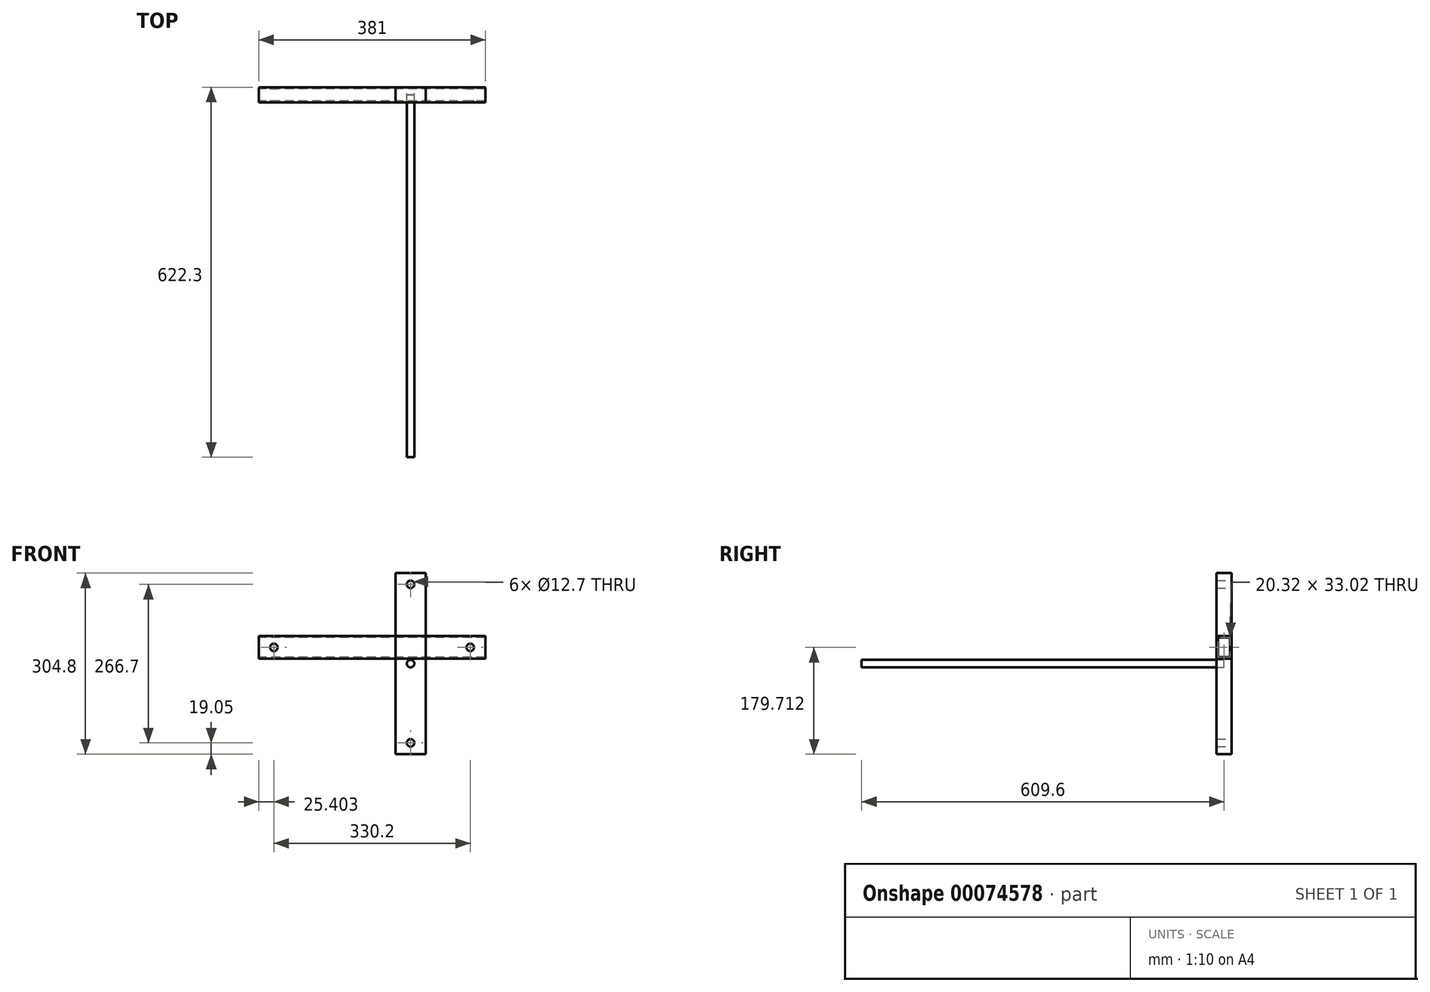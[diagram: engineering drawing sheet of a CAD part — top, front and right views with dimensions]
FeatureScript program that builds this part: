
annotation { "Feature Type Name" : "Feature", "Feature Type Description" : "" }
export const myFeature = defineFeature(function(context is Context, id is Id, definition is map)
    precondition{}
    {
        {
            var Q0;
            Q0=qCreatedBy(makeId("Front.planeOp"),FACE);
            var sketch = newSketch(context, id + "F0", { "sketchPlane" : qUnion([Q0])});
            skLineSegment(sketch, "E0.rect.bottom", {"start": v(25.4, 152.4) * mm, "end": v(-25.4, 152.4) * mm});
            skLineSegment(sketch, "E0.rect.top", {"start": v(25.4, -152.4) * mm, "end": v(-25.4, -152.4) * mm});
            skLineSegment(sketch, "E0.rect.left", {"start": v(25.4, 152.4) * mm, "end": v(25.4, -152.4) * mm});
            skLineSegment(sketch, "E0.rect.right", {"start": v(-25.4, 152.4) * mm, "end": v(-25.4, -152.4) * mm});
            skPoint(sketch, "E0.rect.middle", {"position": v(0, 0) * mm});
            skCircle(sketch, "E1", {"center": v(0, -133.35) * mm, "radius": 6.35 * mm});
            skCircle(sketch, "E2", {"center": v(0, 133.35) * mm, "radius": 6.35 * mm});
            skSolve(sketch);
        }
        {
            var Q0;
            Q0=makeQuery(id+"F0.imprint","IMPRINT",FACE,{"disambiguationData":[TD([[makeQuery(id+"F0.imprint","IMPRINT",EDGE,{"derivedFrom":sQuery(id+"F0.wireOp",EDGE,"E0.rect.bottom")}),1.0]])]});
            extrude(context, id + "F1", {"entities" : qUnion([Q0]), "endBound" : BoundingType.SYMMETRIC, "depth" : 25.4 * mm});
        }
        {
            var Q0;
            Q0=qCreatedBy(makeId("Front.planeOp"),FACE);
            var sketch = newSketch(context, id + "F2", { "sketchPlane" : qUnion([Q0])});
            skLineSegment(sketch, "E3.rect.bottom", {"start": v(125.76, 8.26) * mm, "end": v(-255.24, 8.26) * mm});
            skLineSegment(sketch, "E3.rect.top", {"start": v(125.76, 46.36) * mm, "end": v(-255.24, 46.36) * mm});
            skLineSegment(sketch, "E3.rect.left", {"start": v(125.76, 8.26) * mm, "end": v(125.76, 46.36) * mm});
            skLineSegment(sketch, "E3.rect.right", {"start": v(-255.24, 8.26) * mm, "end": v(-255.24, 46.36) * mm});
            skPoint(sketch, "E3.rect.middle", {"position": v(-64.74, 27.31) * mm});
            skCircle(sketch, "E4", {"center": v(-229.84, 27.31) * mm, "radius": 6.35 * mm});
            skCircle(sketch, "E5", {"center": v(100.36, 27.31) * mm, "radius": 6.35 * mm});
            skSolve(sketch);
        }
        {
            var Q0;
            Q0 = qSketchRegion(id + "F2", true);
            extrude(context, id + "F3", {"entities" : qUnion([Q0]), "endBound" : BoundingType.SYMMETRIC, "depth" : 25.4 * mm});
        }
        {
            var Q0;
            Q0=makeQuery(id+"F3.opExtrude","SWEPT_FACE",FACE,{"disambiguationData":[OSD([sQuery(id+"F2.wireOp",EDGE,"E3.rect.right")])]});
            var Q1;
            Q1=makeQuery(id+"F3.opExtrude","SWEPT_FACE",FACE,{"disambiguationData":[OSD([sQuery(id+"F2.wireOp",EDGE,"E4")])]});
            var Q2;
            Q2=makeQuery(id+"F3.opExtrude","SWEPT_FACE",FACE,{"disambiguationData":[OSD([sQuery(id+"F2.wireOp",EDGE,"E3.rect.left")])]});
            var Q3;
            Q3=makeQuery(id+"F3.opExtrude","SWEPT_FACE",FACE,{"disambiguationData":[OSD([sQuery(id+"F2.wireOp",EDGE,"E5")])]});
            shell(context, id + "F4", {"entities" : qUnion([Q0, Q1, Q2, Q3]), "thickness" : 2.54 * mm});
        }
        {
            var Q0;
            Q0=qCreatedBy(makeId("Front.planeOp"),FACE);
            var sketch = newSketch(context, id + "F5", { "sketchPlane" : qUnion([Q0])});
            skCircle(sketch, "E6", {"center": v(0, 0) * mm, "radius": 6.35 * mm});
            skSolve(sketch);
        }
        {
            var Q0;
            Q0 = qSketchRegion(id + "F5", true);
            extrude(context, id + "F6", {"entities" : qUnion([Q0]), "depth" : 609.6 * mm});
        }
    });
